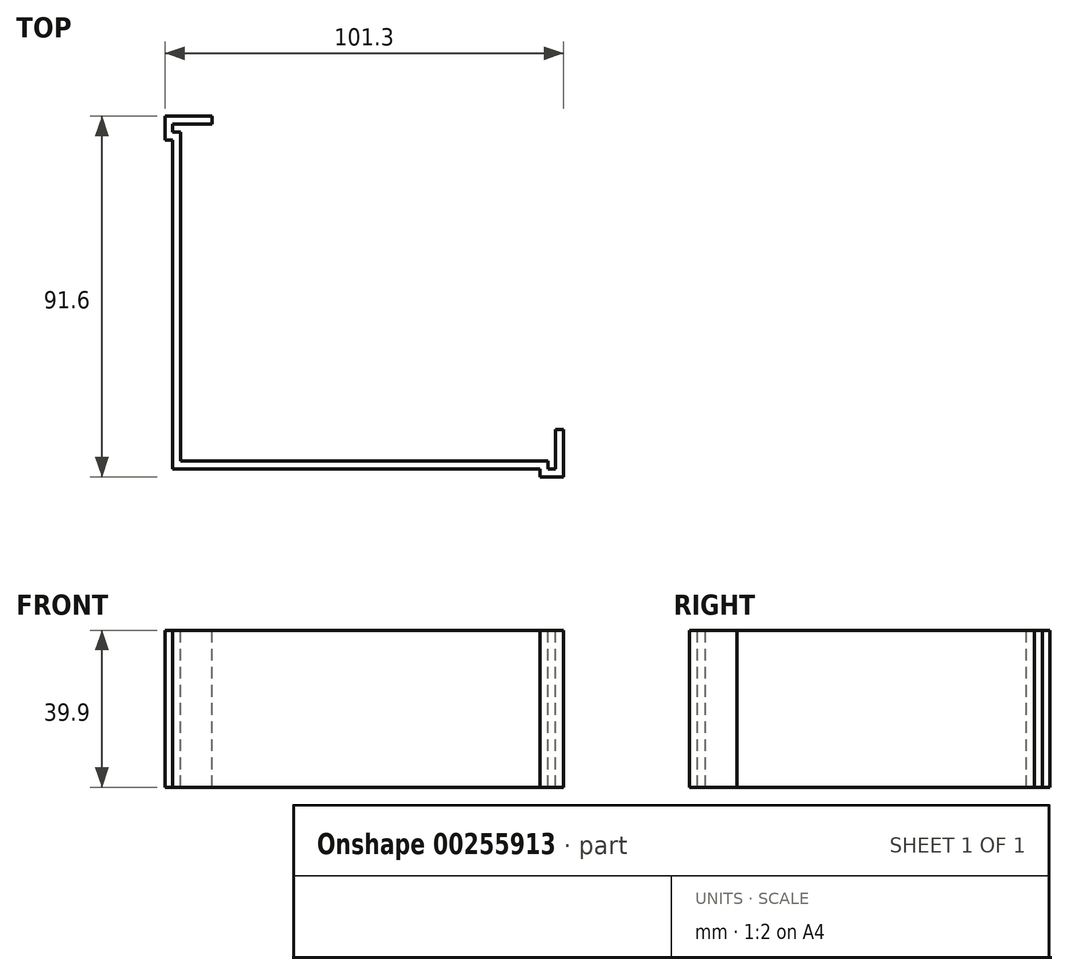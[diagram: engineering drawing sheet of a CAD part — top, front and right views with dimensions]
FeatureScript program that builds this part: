
annotation { "Feature Type Name" : "Feature", "Feature Type Description" : "" }
export const myFeature = defineFeature(function(context is Context, id is Id, definition is map)
    precondition{}
    {
        {
            var Q0;
            Q0=qCreatedBy(makeId("Top.planeOp"),FACE);
            var sketch = newSketch(context, id + "F0", { "sketchPlane" : qUnion([Q0])});
            skLineSegment(sketch, "E0.bottom", {"start": v(50.65, -45.8) * mm, "end": v(-50.65, -45.8) * mm});
            skLineSegment(sketch, "E0.top", {"start": v(50.65, 45.8) * mm, "end": v(-50.65, 45.8) * mm});
            skLineSegment(sketch, "E0.left", {"start": v(50.65, -45.8) * mm, "end": v(50.65, 45.8) * mm});
            skLineSegment(sketch, "E0.right", {"start": v(-50.65, -45.8) * mm, "end": v(-50.65, 45.8) * mm});
            skPoint(sketch, "E0.middle", {"position": v(0, 0) * mm});
            skSolve(sketch);
        }
        {
            var Q0;
            Q0=qSketchRegion(id+"F0",true);
            extrude(context, id + "F1", {"entities" : qUnion([Q0]), "depth" : 39.9 * mm});
        }
        {
            var Q0;
            Q0=makeQuery(id+"F1.opExtrude","CAP_FACE",FACE,{"disambiguationData":[OSD([sQuery(id+"F0.wireOp",EDGE,"E0.bottom"),sQuery(id+"F0.wireOp",EDGE,"E0.top"),sQuery(id+"F0.wireOp",EDGE,"E0.left"),sQuery(id+"F0.wireOp",EDGE,"E0.right")])],"isStart":false});
            var sketch = newSketch(context, id + "F2", { "sketchPlane" : qUnion([Q0])});
            skLineSegment(sketch, "E1", {"start": v(-38.65, 45.8) * mm, "end": v(-38.65, 43.8) * mm});
            skLineSegment(sketch, "E2", {"start": v(-38.65, 43.8) * mm, "end": v(-48.65, 43.8) * mm});
            skLineSegment(sketch, "E3", {"start": v(-46.65, -41.8) * mm, "end": v(46.65, -41.8) * mm});
            skLineSegment(sketch, "E4", {"start": v(48.65, -43.8) * mm, "end": v(48.65, -33.8) * mm});
            skLineSegment(sketch, "E5", {"start": v(48.65, -33.8) * mm, "end": v(50.65, -33.8) * mm});
            skLineSegment(sketch, "E6", {"start": v(-38.65, 45.8) * mm, "end": v(50.65, 45.8) * mm});
            skLineSegment(sketch, "E7", {"start": v(50.65, 45.8) * mm, "end": v(50.65, -33.8) * mm});
            skLineSegment(sketch, "E8", {"start": v(-46.65, 41.8) * mm, "end": v(-46.65, -41.8) * mm});
            skLineSegment(sketch, "E9", {"start": v(-48.65, 43.8) * mm, "end": v(-48.65, 41.8) * mm});
            skLineSegment(sketch, "E10", {"start": v(-48.65, 41.8) * mm, "end": v(-46.65, 41.8) * mm});
            skLineSegment(sketch, "E11", {"start": v(46.65, -41.8) * mm, "end": v(46.65, -43.8) * mm});
            skLineSegment(sketch, "E12", {"start": v(46.65, -43.8) * mm, "end": v(48.65, -43.8) * mm});
            skSolve(sketch);
        }
        {
            var Q0;
            Q0=qSketchRegion(id+"F2",true);
            extrude(context, id + "F3", {"entities" : qUnion([Q0]), "operationType" : NewBodyOperationType.REMOVE, "oppositeDirection" : true, "depth" : 39.9 * mm});
        }
        {
            var Q0;
            Q0=makeQuery(id+"F1.opExtrude","CAP_FACE",FACE,{"disambiguationData":[OSD([sQuery(id+"F0.wireOp",EDGE,"E0.bottom"),sQuery(id+"F0.wireOp",EDGE,"E0.top"),sQuery(id+"F0.wireOp",EDGE,"E0.left"),sQuery(id+"F0.wireOp",EDGE,"E0.right")])],"isStart":true});
            var sketch = newSketch(context, id + "F4", { "sketchPlane" : qUnion([Q0])});
            skLineSegment(sketch, "E13.bottom", {"start": v(45.65, -40.8) * mm, "end": v(-45.65, -40.8) * mm});
            skLineSegment(sketch, "E13.top", {"start": v(45.65, 40.8) * mm, "end": v(-45.65, 40.8) * mm});
            skLineSegment(sketch, "E13.left", {"start": v(45.65, -40.8) * mm, "end": v(45.65, 40.8) * mm});
            skLineSegment(sketch, "E13.right", {"start": v(-45.65, -40.8) * mm, "end": v(-45.65, 40.8) * mm});
            skPoint(sketch, "E13.middle", {"position": v(0, 0) * mm});
            skSolve(sketch);
        }
        {
            var Q0;
            Q0 = qSketchRegion(id + "F4", true);
            extrude(context, id + "F5", {"entities" : qUnion([Q0]), "operationType" : NewBodyOperationType.REMOVE, "oppositeDirection" : true, "depth" : 25 * mm});
        }
        {
            var Q0;
            Q0=makeQuery(id+"F1.opExtrude","CAP_FACE",FACE,{"disambiguationData":[OSD([sQuery(id+"F0.wireOp",EDGE,"E0.bottom"),sQuery(id+"F0.wireOp",EDGE,"E0.top"),sQuery(id+"F0.wireOp",EDGE,"E0.left"),sQuery(id+"F0.wireOp",EDGE,"E0.right")])],"isStart":false});
            var sketch = newSketch(context, id + "F6", { "sketchPlane" : qUnion([Q0])});
            skLineSegment(sketch, "E14", {"start": v(-50.65, 39.8) * mm, "end": v(-48.65, 39.8) * mm});
            skLineSegment(sketch, "E15", {"start": v(-48.65, 39.8) * mm, "end": v(-48.65, -43.8) * mm});
            skLineSegment(sketch, "E16", {"start": v(-48.65, -43.8) * mm, "end": v(44.65, -43.8) * mm});
            skLineSegment(sketch, "E17", {"start": v(44.65, -43.8) * mm, "end": v(44.65, -45.8) * mm});
            skLineSegment(sketch, "E18", {"start": v(44.65, -45.8) * mm, "end": v(-50.65, -45.8) * mm});
            skLineSegment(sketch, "E19", {"start": v(-50.65, -45.8) * mm, "end": v(-50.65, 39.8) * mm});
            skSolve(sketch);
        }
        {
            var Q0;
            Q0 = qSketchRegion(id + "F6", true);
            extrude(context, id + "F7", {"entities" : qUnion([Q0]), "operationType" : NewBodyOperationType.REMOVE, "oppositeDirection" : true, "depth" : 40 * mm});
        }
    });
